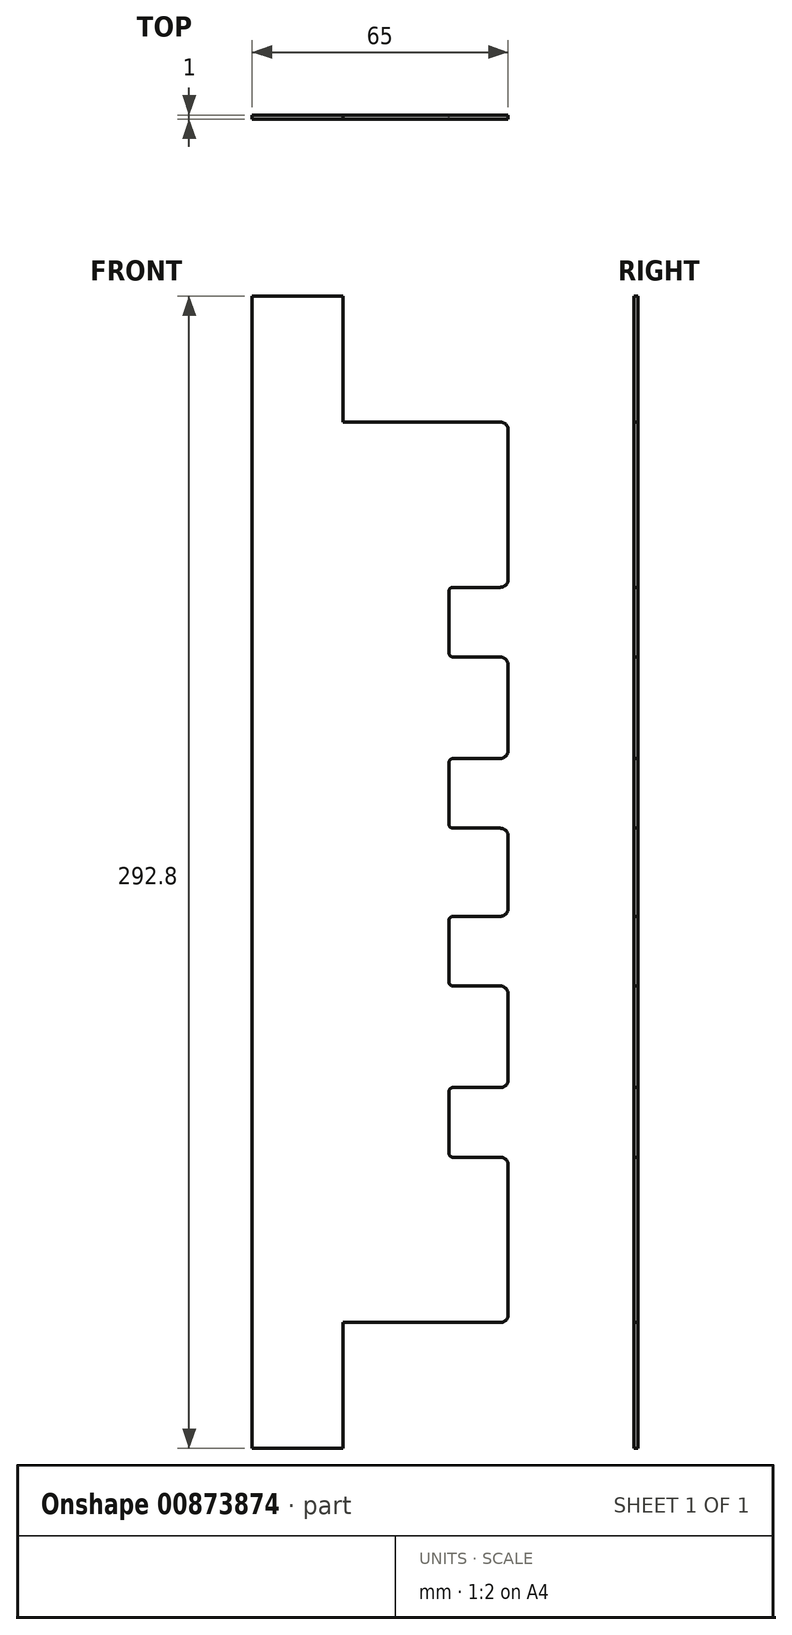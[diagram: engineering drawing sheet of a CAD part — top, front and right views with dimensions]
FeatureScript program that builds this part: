
annotation { "Feature Type Name" : "Feature", "Feature Type Description" : "" }
export const myFeature = defineFeature(function(context is Context, id is Id, definition is map)
    precondition{}
    {
        {
            var Q0;
            Q0=qCreatedBy(makeId("Front.planeOp"),FACE);
            var sketch = newSketch(context, id + "F0", { "sketchPlane" : qUnion([Q0])});
            skLineSegment(sketch, "E0", {"start": v(0, 0) * mm, "end": v(0, 9.2) * mm});
            skLineSegment(sketch, "E1", {"start": v(-2, 11.2) * mm, "end": v(-14, 11.2) * mm});
            skLineSegment(sketch, "E2", {"start": v(-15, 12.2) * mm, "end": v(-15, 27.9) * mm});
            skLineSegment(sketch, "E3", {"start": v(-14, 28.9) * mm, "end": v(-2, 28.9) * mm});
            skLineSegment(sketch, "E4", {"start": v(0, 30.9) * mm, "end": v(0, 52.7) * mm});
            skLineSegment(sketch, "E5", {"start": v(-2, 54.7) * mm, "end": v(-14, 54.7) * mm});
            skLineSegment(sketch, "E6", {"start": v(-15, 55.7) * mm, "end": v(-15, 71.4) * mm});
            skLineSegment(sketch, "E7", {"start": v(-14, 72.4) * mm, "end": v(-2, 72.4) * mm});
            skLineSegment(sketch, "E8", {"start": v(0, 74.4) * mm, "end": v(0, 112.4) * mm});
            skLineSegment(sketch, "E9", {"start": v(-2, 114.4) * mm, "end": v(-42, 114.4) * mm});
            skLineSegment(sketch, "E10", {"start": v(-42, 114.4) * mm, "end": v(-42, 146.4) * mm});
            skLineSegment(sketch, "E11", {"start": v(-42, 146.4) * mm, "end": v(-65, 146.4) * mm});
            skLineSegment(sketch, "E12", {"start": v(-65, 146.4) * mm, "end": v(-65, 0) * mm});
            skPoint(sketch, "E13.visualSharp", {"position": v(0, 72.4) * mm});
            skArc(sketch, "E13.filletArc", {"start": v(-2, 72.4) * mm, "mid": v(-0.59, 72.99) * mm, "end": v(0, 74.4) * mm});
            skPoint(sketch, "E14.visualSharp", {"position": v(0, 54.7) * mm});
            skArc(sketch, "E14.filletArc", {"start": v(0, 52.7) * mm, "mid": v(-0.59, 54.11) * mm, "end": v(-2, 54.7) * mm});
            skPoint(sketch, "E15.visualSharp", {"position": v(0, 28.9) * mm});
            skArc(sketch, "E15.filletArc", {"start": v(-2, 28.9) * mm, "mid": v(-0.59, 29.49) * mm, "end": v(0, 30.9) * mm});
            skPoint(sketch, "E16.visualSharp", {"position": v(0, 11.2) * mm});
            skArc(sketch, "E16.filletArc", {"start": v(0, 9.2) * mm, "mid": v(-0.59, 10.61) * mm, "end": v(-2, 11.2) * mm});
            skPoint(sketch, "E17.visualSharp", {"position": v(-15, 11.2) * mm});
            skArc(sketch, "E17.filletArc", {"start": v(-15, 12.2) * mm, "mid": v(-14.7, 11.5) * mm, "end": v(-14, 11.2) * mm});
            skPoint(sketch, "E18.visualSharp", {"position": v(-15, 28.9) * mm});
            skArc(sketch, "E18.filletArc", {"start": v(-14, 28.9) * mm, "mid": v(-14.7, 28.6) * mm, "end": v(-15, 27.9) * mm});
            skPoint(sketch, "E19.visualSharp", {"position": v(-15, 54.7) * mm});
            skArc(sketch, "E19.filletArc", {"start": v(-15, 55.7) * mm, "mid": v(-14.7, 55) * mm, "end": v(-14, 54.7) * mm});
            skPoint(sketch, "E20.visualSharp", {"position": v(-15, 72.4) * mm});
            skArc(sketch, "E20.filletArc", {"start": v(-14, 72.4) * mm, "mid": v(-14.7, 72.1) * mm, "end": v(-15, 71.4) * mm});
            skPoint(sketch, "E21.visualSharp", {"position": v(0, 114.4) * mm});
            skArc(sketch, "E21.filletArc", {"start": v(0, 112.4) * mm, "mid": v(-0.59, 113.81) * mm, "end": v(-2, 114.4) * mm});
            skLineSegment(sketch, "E22", {"start": v(-15, 63.55) * mm, "end": v(5.94, 63.55) * mm, "construction": true});
            skLineSegment(sketch, "E23", {"start": v(-15, 20.05) * mm, "end": v(5.76, 20.05) * mm, "construction": true});
            skArc(sketch, "E24.MirrorCS", {"start": v(-14, -72.4) * mm, "mid": v(-14.7, -72.1) * mm, "end": v(-15, -71.4) * mm});
            skArc(sketch, "E25.MirrorCS", {"start": v(-14, -28.9) * mm, "mid": v(-14.7, -28.6) * mm, "end": v(-15, -27.9) * mm});
            skArc(sketch, "E26.MirrorCS", {"start": v(-15, -55.7) * mm, "mid": v(-14.7, -55) * mm, "end": v(-14, -54.7) * mm});
            skArc(sketch, "E27.MirrorCS", {"start": v(-15, -12.2) * mm, "mid": v(-14.7, -11.5) * mm, "end": v(-14, -11.2) * mm});
            skArc(sketch, "E28.MirrorCS", {"start": v(-2, -28.9) * mm, "mid": v(-0.59, -29.49) * mm, "end": v(0, -30.9) * mm});
            skLineSegment(sketch, "E29.MirrorCS", {"start": v(-2, -11.2) * mm, "end": v(-14, -11.2) * mm});
            skArc(sketch, "E30.MirrorCS", {"start": v(0, -52.7) * mm, "mid": v(-0.59, -54.11) * mm, "end": v(-2, -54.7) * mm});
            skArc(sketch, "E31.MirrorCS", {"start": v(0, -112.4) * mm, "mid": v(-0.59, -113.81) * mm, "end": v(-2, -114.4) * mm});
            skArc(sketch, "E32.MirrorCS", {"start": v(-2, -72.4) * mm, "mid": v(-0.59, -72.99) * mm, "end": v(0, -74.4) * mm});
            skLineSegment(sketch, "E33.MirrorCS", {"start": v(0, 0) * mm, "end": v(0, -9.2) * mm});
            skArc(sketch, "E34.MirrorCS", {"start": v(0, -9.2) * mm, "mid": v(-0.59, -10.61) * mm, "end": v(-2, -11.2) * mm});
            skLineSegment(sketch, "E35.MirrorCS", {"start": v(-15, -12.2) * mm, "end": v(-15, -27.9) * mm});
            skLineSegment(sketch, "E36.MirrorCS", {"start": v(-14, -28.9) * mm, "end": v(-2, -28.9) * mm});
            skLineSegment(sketch, "E37.MirrorCS", {"start": v(-2, -54.7) * mm, "end": v(-14, -54.7) * mm});
            skLineSegment(sketch, "E38.MirrorCS", {"start": v(-14, -72.4) * mm, "end": v(-2, -72.4) * mm});
            skLineSegment(sketch, "E39.MirrorCS", {"start": v(-15, -55.7) * mm, "end": v(-15, -71.4) * mm});
            skLineSegment(sketch, "E40.MirrorCS", {"start": v(-15, -20.05) * mm, "end": v(5.76, -20.05) * mm, "construction": true});
            skLineSegment(sketch, "E41.MirrorCS", {"start": v(-15, -63.55) * mm, "end": v(5.94, -63.55) * mm, "construction": true});
            skPoint(sketch, "E42.MirrorP", {"position": v(-15, -11.2) * mm});
            skPoint(sketch, "E43.MirrorP", {"position": v(0, -11.2) * mm});
            skPoint(sketch, "E44.MirrorP", {"position": v(0, -28.9) * mm});
            skLineSegment(sketch, "E45.MirrorCS", {"start": v(-42, -146.4) * mm, "end": v(-65, -146.4) * mm});
            skPoint(sketch, "E46.MirrorP", {"position": v(-15, -54.7) * mm});
            skLineSegment(sketch, "E47.MirrorCS", {"start": v(0, -74.4) * mm, "end": v(0, -112.4) * mm});
            skLineSegment(sketch, "E48.MirrorCS", {"start": v(-42, -114.4) * mm, "end": v(-42, -146.4) * mm});
            skPoint(sketch, "E49.MirrorP", {"position": v(-15, -28.9) * mm});
            skLineSegment(sketch, "E50.MirrorCS", {"start": v(-65, -146.4) * mm, "end": v(-65, 0) * mm});
            skPoint(sketch, "E51.MirrorP", {"position": v(0, -54.7) * mm});
            skLineSegment(sketch, "E52.MirrorCS", {"start": v(-2, -114.4) * mm, "end": v(-42, -114.4) * mm});
            skPoint(sketch, "E53.MirrorP", {"position": v(0, -114.4) * mm});
            skPoint(sketch, "E54.MirrorP", {"position": v(0, -72.4) * mm});
            skLineSegment(sketch, "E55.MirrorCS", {"start": v(0, -30.9) * mm, "end": v(0, -52.7) * mm});
            skPoint(sketch, "E56.MirrorP", {"position": v(-15, -72.4) * mm});
            skSolve(sketch);
        }
        {
            var Q0;
            Q0=makeQuery(id+"F0.imprint","IMPRINT",FACE,{"disambiguationData":[TD([[makeQuery(id+"F0.imprint","IMPRINT",EDGE,{"derivedFrom":sQuery(id+"F0.wireOp",EDGE,"E0")}),1.0]])]});
            extrude(context, id + "F1", {"entities" : qUnion([Q0]), "depth" : 1 * mm, "offsetDistance" : 25 * mm});
        }
    });
